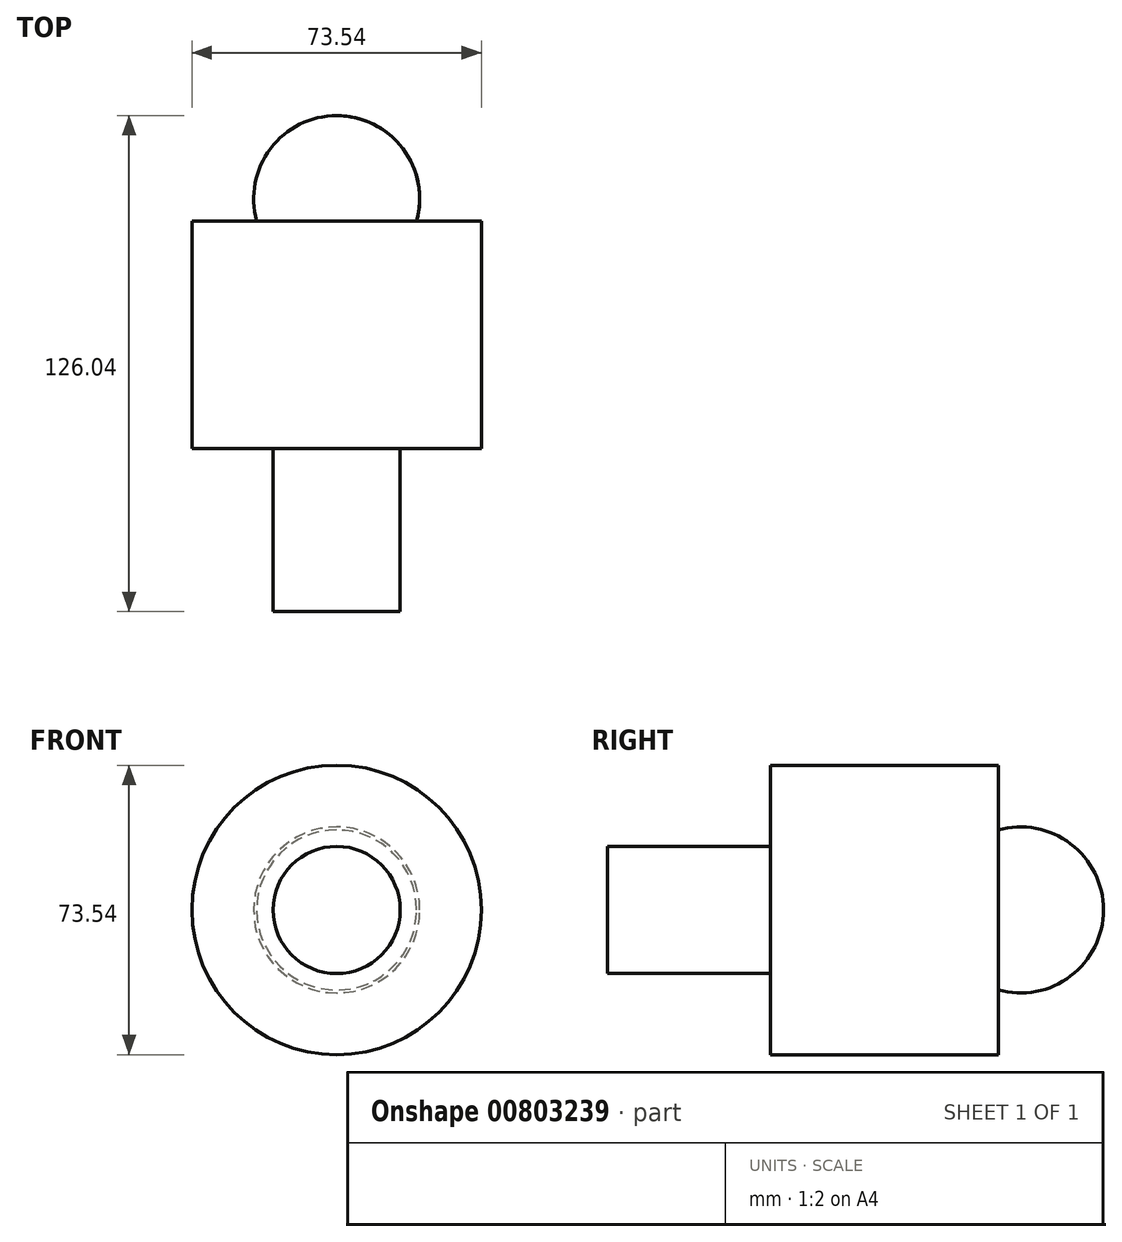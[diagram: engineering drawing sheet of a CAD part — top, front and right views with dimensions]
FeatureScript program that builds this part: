
annotation { "Feature Type Name" : "Feature", "Feature Type Description" : "" }
export const myFeature = defineFeature(function(context is Context, id is Id, definition is map)
    precondition{}
    {
        {
            var Q0;
            Q0=qCreatedBy(makeId("Top.planeOp"),FACE);
            var sketch = newSketch(context, id + "F0", { "sketchPlane" : qUnion([Q0])});
            skLineSegment(sketch, "E0", {"start": v(0, 0) * mm, "end": v(0, 76.83) * mm, "construction": true});
            skLineSegment(sketch, "E1", {"start": v(0, 76.83) * mm, "end": v(0, 0) * mm, "construction": true});
            skLineSegment(sketch, "E2", {"start": v(0, 0) * mm, "end": v(0, -76.1) * mm, "construction": true});
            skLineSegment(sketch, "E3.bottom", {"start": v(20.33, 46.72) * mm, "end": v(36.77, 46.72) * mm});
            skLineSegment(sketch, "E3.top", {"start": v(16.15, -11.13) * mm, "end": v(36.77, -11.13) * mm});
            skLineSegment(sketch, "E3.left", {"start": v(0, 46.72) * mm, "end": v(0, -11.13) * mm});
            skLineSegment(sketch, "E3.right", {"start": v(36.77, 46.72) * mm, "end": v(36.77, -11.13) * mm});
            skArc(sketch, "E4", {"start": v(20.33, 46.72) * mm, "mid": v(16.8, 65.14) * mm, "end": v(0, 73.48) * mm});
            skLineSegment(sketch, "E5.top", {"start": v(0, -52.56) * mm, "end": v(16.15, -52.56) * mm});
            skLineSegment(sketch, "E5.right", {"start": v(16.15, -11.13) * mm, "end": v(16.15, -52.56) * mm});
            skLineSegment(sketch, "E6", {"start": v(0, 73.48) * mm, "end": v(0, -52.56) * mm});
            skSolve(sketch);
        }
        {
            var Q0;
            Q0=makeQuery(id+"F0.imprint","IMPRINT",FACE,{"disambiguationData":[TD([[makeQuery(id+"F0.imprint","IMPRINT",EDGE,{"derivedFrom":sQuery(id+"F0.wireOp",EDGE,"E3.bottom")}),-1.0]])]});
            var Q1;
            Q1=sQuery(id+"F0.wireOp",EDGE,"E6");
            revolve(context, id + "F1", {"surfaceOperationType" : NewSurfaceOperationType.NEW, "entities" : qUnion([Q0]), "axis" : qUnion([Q1]), "revolveType" : RevolveType.FULL});
        }
    });
